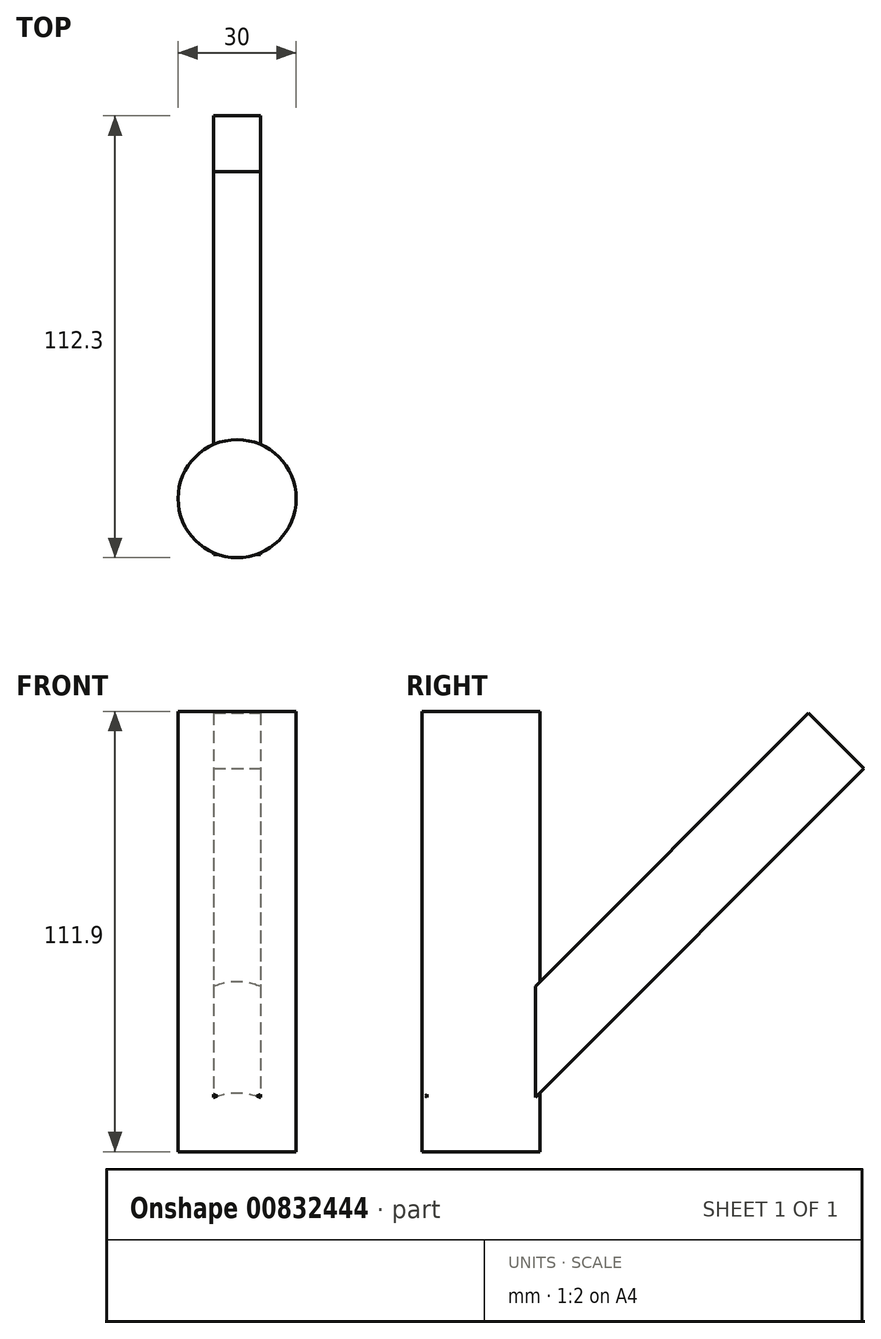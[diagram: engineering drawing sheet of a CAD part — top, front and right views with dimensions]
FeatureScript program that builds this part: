
annotation { "Feature Type Name" : "Feature", "Feature Type Description" : "" }
export const myFeature = defineFeature(function(context is Context, id is Id, definition is map)
    precondition{}
    {
        {
            var Q0;
            Q0=qCreatedBy(makeId("Top.planeOp"),FACE);
            var sketch = newSketch(context, id + "F0", { "sketchPlane" : qUnion([Q0])});
            skCircle(sketch, "E0", {"center": v(0, 0) * mm, "radius": 15 * mm});
            skSolve(sketch);
        }
        {
            var Q0;
            Q0=makeQuery(id+"F0.imprint","IMPRINT",FACE,{"disambiguationData":[TD([[makeQuery(id+"F0.imprint","IMPRINT",EDGE,{"derivedFrom":sQuery(id+"F0.wireOp",EDGE,"E0")}),1.0]])]});
            extrude(context, id + "F1", {"entities" : qUnion([Q0]), "depth" : 111.9 * mm, "offsetDistance" : 25 * mm});
        }
        {
            var Q0;
            Q0=qCreatedBy(makeId("Front.planeOp"),FACE);
            var Q1;
            Q1=qCreatedBy(makeId("Top.planeOp"),FACE);
            cPlane(context, id + "F2", {"entities" : qUnion([Q0, Q1]), "cplaneType" : CPlaneType.MID_PLANE, "offset" : 25 * mm, "width" : 150 * mm, "height" : 150 * mm});
        }
        {
            var Q0;
            Q0=qCreatedBy(id+"F2.planeOp",FACE);
            var sketch = newSketch(context, id + "F3", { "sketchPlane" : qUnion([Q0])});
            skLineSegment(sketch, "E1.bottom", {"start": v(-6, 20) * mm, "end": v(6, 20) * mm});
            skLineSegment(sketch, "E1.top", {"start": v(-6, 0) * mm, "end": v(6, 0) * mm});
            skLineSegment(sketch, "E1.left", {"start": v(-6, 20) * mm, "end": v(-6, 0) * mm});
            skLineSegment(sketch, "E1.right", {"start": v(6, 20) * mm, "end": v(6, 0) * mm});
            skSolve(sketch);
        }
        {
            var Q0;
            Q0 = qSketchRegion(id + "F3", true);
            extrude(context, id + "F4", {"entities" : qUnion([Q0]), "operationType" : NewBodyOperationType.ADD, "oppositeDirection" : true, "depth" : 137.6 * mm, "offsetDistance" : 25 * mm});
        }
    });
